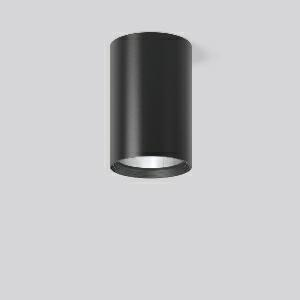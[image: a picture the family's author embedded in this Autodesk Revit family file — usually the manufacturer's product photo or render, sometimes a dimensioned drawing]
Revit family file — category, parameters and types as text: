
# Revit family: heledon_maxi_a_931232_003_76_683f
name_source: partatom
category: Lighting Fixtures
units: mm (PartAtom-declared; Revit-internal decimal feet)

## family parameters
Cut with Voids When Loaded = No
Host = Face
Light Source = No
Part Type = Normal
Room Calculation Point = No
Round Connector Dimension = Use Diameter
Shared = No

## types (1)
- HELEDON maxi A (1 x LED Modul 932 fresh meat, 2150 lm, 3200)
    Apparent Load = 33 VA
    Approval mark = CE
    CIE Flux Codes = 100 100 100 100 100
    Color Rendering = 90
    Color Temperature = 3200
    Default Elevation = 1800 mm
    Description = Series: HELEDON maxi
Cylindrical surface-mounted downlight. Housing: die-cast aluminium, powder-coated. Internal ceiling frame polycarbonate with bayonet mounting. Black plastic ring and recessed LED to prevent glare from the side. Optical assembly with reflector made of MIRO-Silver with 98% total light reflection for outstanding efficiency - can be changed without tools. Special LED for illumination of meat included. Suitable for Ceiling mounting. Easy installation with a separate ceiling frame with bayonet mounting and plug connection. Driver integrated. Connected via plug-in connector. High quality converter without flickering and stroboscopic effect. The following accessories can be mounted without use of tools: interchangeable lenses, decorative glasses, honeycomb louvre, clear and frosted diffusers, white interchangeable plastic ring. 
Colour: deep black, matt (RAL 9005)
Diameter: 123 mm
Height: 183 mm
Lamp: LED
Socket: without socket
Colour temperature: fresh meat
System power: 33 W
Rated luminous flux: 2150 lm
Luminous efficiency: 65 lm/W
Control gear: Converter, dimmable, DALI
Protection class: I
Type of protection: IP 20
    Height = 183 mm
    Lamp = 1 x LED Modul 932 fresh meat
    Lamp Light Flux = 2150 lm
    Lamp count = 1
    Length = 123 mm
    Lifetime = 50000 h
    Luminous efficacy = 65 lm/W
    Manufacturer = RZB
    ModVariant = No
    Model = 931232.003.76
    Mounting Place = Ceiling
    Mounting Type = Surface mounted
    Number of Poles = 1
    OnlyDefault = Yes
    Power Factor = 1
    Product Name = HELEDON maxi A
    Product group = Surface mounted downlights
    ProductGroupID = 302
    Protection Class = Protection class I
    Protection Degree = IP 20
    RLX_Detail_Level = 1
    RLX_Emergency_Light_Flux = 0 lm
    RLX_Emergency_Type = 0
    RLX_Emergency_Type_DB = No
    RlxData = <blob elided: 99417 chars, md5=fe4f0466>
    Socket = socket
    Standby Power = 0 W
    System Light Flux = 2150 lm
    System Power = 33 W
    Type Comments = Product without accessories
    Type Image = 931192.003.jpg
    URL = http://relux.com
    VarID = ---
    Voltage = 230 V
    Voltage Range = 220-240 V
    Weight = 0.00 kg
    Width = 0 mm  [stored 0 ft]

note: [stored X ft] marks values corroborated as IEEE doubles in the binary element streams (Revit-internal decimal feet)

## geometry (parser evidence)
native form markers: Blend x4, Sweep x9
no freeform markers — native parametric forms only
